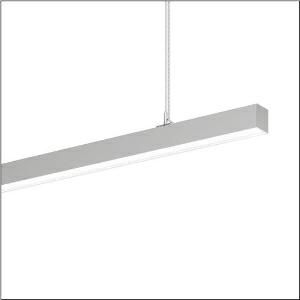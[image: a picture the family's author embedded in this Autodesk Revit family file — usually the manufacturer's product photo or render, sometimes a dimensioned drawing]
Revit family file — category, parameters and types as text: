
# Revit family: silica_r__21_51mx33db39sb_b1fc
name_source: partatom
category: Lighting Fixtures
units: mm (PartAtom-declared; Revit-internal decimal feet)

## family parameters
Cut with Voids When Loaded = No
Host = Face
Light Source = No
Part Type = Normal
Room Calculation Point = No
Round Connector Dimension = Use Diameter
Shared = No

## types (1)
- --- (1 x LED, 7390 lm, 51.6 W, 3000K)
    Apparent Load = 52 VA
    CIE Flux Codes = 78 96 99 55 100
    Color Rendering = 80
    Color Temperature = 3000K
    Default Elevation = 1800 mm
    Description = Silica® 21, office luminaire, primary optical cover: prismatic diffuser, of PMMA, CAT 2 (L<= 3000cd/m²), light emission: direct/indirect distribution, primary light characteristic: symmetric, installation type: suspended mounting, LED, rated luminous flux: 7.390lm, luminous efficacy: 143lm/W, light colour: 830, colour temperature: 3000K, control gear: DALI 2, with terminal, 3+2-pole, max. 2.5mm², mains connection: 220..240V, AC, 50/60Hz, rated input power: 51.6W, luminaire housing, of aluminium, metallic grey (RAL 9006), length: 1.504mm, width: 53mm, height: 53mm, protection rating (complete): IP20, insulation class (complete): insulation class I (protective earthing), certification: CE, permissible operating ambient temperature: 0..+35°C, standard: EN 50419, packaging unit: 1 piece
    Height = 53 mm
    Lamp = 1 x LED
    Lamp Light Flux = 7390 lm
    Lamp Power = 51.6 W
    Lamp count = 1
    Length = 1504 mm
    Luminous efficacy = 143 lm/W
    Manufacturer = Siteco
    ModVariant = No
    Model = 51MX33DB39SB
    Mounting Place = Ceiling
    Mounting Type = Pendant
    Number of Poles = 1
    OnlyDefault = Yes
    Power Factor = 1
    Product Name = Silica® 21
    Product group = office luminaire | ceiling pendant
    ProductGroupID = 903
    Protection Class = Protection class I
    Protection Degree = IP 20
    RLX_Detail_Level = 1
    RLX_Emergency_Light_Flux = 0 lm
    RLX_Emergency_Type = 0
    RLX_Emergency_Type_DB = No
    RlxData = <blob elided: 23537 chars, md5=7554843a>
    Socket = socket
    Standby Power = 0 W
    System Light Flux = 7390 lm
    System Power = 52 W
    Type Comments = factory setting: luminous flux: 100 % | dim-lin: 254 | 345 mA
    Type Image = l_1335864.jpg
    URL = http://relux.com
    VarID = @adj_122243
    Voltage = 0 V
    Weight = 0.00 kg
    Width = 53 mm

## geometry (parser evidence)
native form markers: Blend x4, Sweep x11
no freeform markers — native parametric forms only
